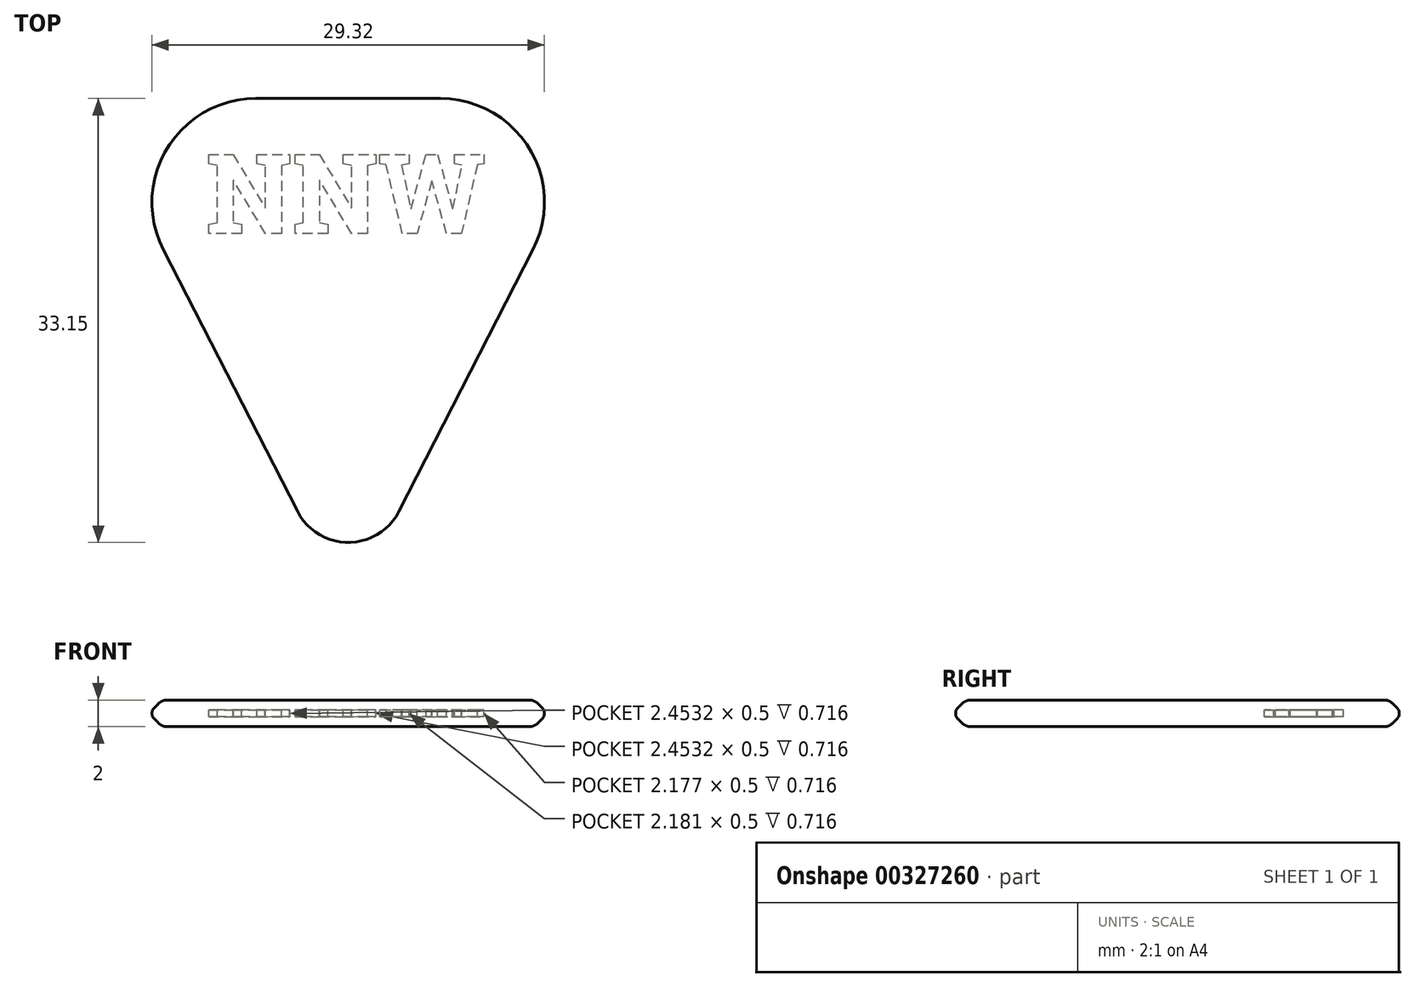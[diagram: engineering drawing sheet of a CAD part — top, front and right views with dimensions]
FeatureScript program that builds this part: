
annotation { "Feature Type Name" : "Feature", "Feature Type Description" : "" }
export const myFeature = defineFeature(function(context is Context, id is Id, definition is map)
    precondition{}
    {
        {
            var Q0;
            Q0=qCreatedBy(makeId("Top.planeOp"),FACE);
            var sketch = newSketch(context, id + "F0", { "sketchPlane" : qUnion([Q0])});
            skLineSegment(sketch, "E0", {"start": v(-6.9, 12.45) * mm, "end": v(6.9, 12.45) * mm});
            skLineSegment(sketch, "E1", {"start": v(14.03, 0.8) * mm, "end": v(4, -18.74) * mm});
            skLineSegment(sketch, "E2", {"start": v(-4, -18.74) * mm, "end": v(-14.03, 0.8) * mm});
            skPoint(sketch, "E3.visualSharp", {"position": v(-20, 12.45) * mm});
            skArc(sketch, "E3.filletArc", {"start": v(-6.9, 12.45) * mm, "mid": v(-13.73, 8.63) * mm, "end": v(-14.03, 0.8) * mm});
            skPoint(sketch, "E4.visualSharp", {"position": v(20, 12.45) * mm});
            skArc(sketch, "E4.filletArc", {"start": v(14.03, 0.8) * mm, "mid": v(13.73, 8.63) * mm, "end": v(6.9, 12.45) * mm});
            skPoint(sketch, "E5.visualSharp", {"position": v(0, -26.55) * mm});
            skArc(sketch, "E5.filletArc", {"start": v(-4, -18.74) * mm, "mid": v(0, -21.18) * mm, "end": v(4, -18.74) * mm});
            skSolve(sketch);
        }
        {
            var Q0;
            Q0=makeQuery(id+"F0.imprint","IMPRINT",FACE,{"disambiguationData":[TD([[makeQuery(id+"F0.imprint","IMPRINT",EDGE,{"derivedFrom":sQuery(id+"F0.wireOp",EDGE,"E0")}),-1.0]])]});
            extrude(context, id + "F1", {"entities" : qUnion([Q0]), "endBound" : BoundingType.SYMMETRIC, "depth" : 2 * mm});
        }
        {
            var Q0;
            Q0=makeQuery(id+"F1.opExtrude","CAP_EDGE",EDGE,{"disambiguationData":[OSD([sQuery(id+"F0.wireOp",EDGE,"E1")])],"isStart":false});
            var Q1;
            Q1=makeQuery(id+"F1.opExtrude","CAP_EDGE",EDGE,{"disambiguationData":[OSD([sQuery(id+"F0.wireOp",EDGE,"E1")])],"isStart":true});
            chamfer(context, id + "F2", {"entities" : qUnion([Q0, Q1]), "chamferType" : ChamferType.OFFSET_ANGLE, "width" : 1 * mm, "oppositeDirection" : false, "angle" : 45 * degree, "tangentPropagation" : true});
        }
        {
            var Q0;
            {var subQ0=sQuery(id+"F0.wireOp",EDGE,"E2");Q0=makeQuery(id+"F2.opChamfer","BLEND_EDGE",EDGE,{"blendedFrom":[makeQuery(id+"F1.opExtrude","CAP_EDGE",EDGE,{"disambiguationData":[OSD([subQ0])],"isStart":false}),makeQuery(id+"F1.opExtrude","CAP_FACE",FACE,{"disambiguationData":[OSD([sQuery(id+"F0.wireOp",EDGE,"E0"),sQuery(id+"F0.wireOp",EDGE,"E1"),subQ0,sQuery(id+"F0.wireOp",EDGE,"E3.filletArc"),sQuery(id+"F0.wireOp",EDGE,"E4.filletArc"),sQuery(id+"F0.wireOp",EDGE,"E5.filletArc")])],"isStart":false})],"blendedInto":[makeQuery(id+"F1.opExtrude","CAP_FACE",FACE,{"disambiguationData":[OSD([sQuery(id+"F0.wireOp",EDGE,"E0"),sQuery(id+"F0.wireOp",EDGE,"E1"),subQ0,sQuery(id+"F0.wireOp",EDGE,"E3.filletArc"),sQuery(id+"F0.wireOp",EDGE,"E4.filletArc"),sQuery(id+"F0.wireOp",EDGE,"E5.filletArc")])],"isStart":false})]});}
            var Q1;
            {var subQ0=sQuery(id+"F0.wireOp",EDGE,"E1");Q1=makeQuery(id+"F2.opChamfer","BLEND_EDGE",EDGE,{"blendedFrom":[makeQuery(id+"F1.opExtrude","CAP_EDGE",EDGE,{"disambiguationData":[OSD([subQ0])],"isStart":true}),makeQuery(id+"F1.opExtrude","CAP_FACE",FACE,{"disambiguationData":[OSD([sQuery(id+"F0.wireOp",EDGE,"E0"),subQ0,sQuery(id+"F0.wireOp",EDGE,"E2"),sQuery(id+"F0.wireOp",EDGE,"E3.filletArc"),sQuery(id+"F0.wireOp",EDGE,"E4.filletArc"),sQuery(id+"F0.wireOp",EDGE,"E5.filletArc")])],"isStart":true})],"blendedInto":[makeQuery(id+"F1.opExtrude","CAP_FACE",FACE,{"disambiguationData":[OSD([sQuery(id+"F0.wireOp",EDGE,"E0"),subQ0,sQuery(id+"F0.wireOp",EDGE,"E2"),sQuery(id+"F0.wireOp",EDGE,"E3.filletArc"),sQuery(id+"F0.wireOp",EDGE,"E4.filletArc"),sQuery(id+"F0.wireOp",EDGE,"E5.filletArc")])],"isStart":true})]});}
            fillet(context, id + "F3", {"entities" : qUnion([Q0, Q1]), "radius" : 1 * mm, "tangentPropagation" : true, "allowEdgeOverflow" : false});
        }
        {
            var Q0;
            Q0=qCreatedBy(makeId("Top.planeOp"),FACE);
            var sketch = newSketch(context, id + "F4", { "sketchPlane" : qUnion([Q0])});
            skText(sketch, "E6", { "text": "NNW", "fontName": "RobotoSlab-Bold.ttf"});
            const initialGuessF4  = {"E6": [-0.01064, 0.00212, 1, 0, 0.006]};
            skSetInitialGuess(sketch, initialGuessF4);
            skSolve(sketch);
        }
        {
            var Q0;
            Q0=qSketchRegion(id+"F4",true);
            extrude(context, id + "F5", {"entities" : qUnion([Q0]), "operationType" : NewBodyOperationType.REMOVE, "endBound" : BoundingType.SYMMETRIC, "oppositeDirection" : true, "depth" : 0.5 * mm});
        }
        {
            var Q0;
            {var subQ0=sQuery(id+"F0.wireOp",EDGE,"E2");Q0=makeQuery(id+"F2.opChamfer","BLEND_EDGE",EDGE,{"blendedFrom":[makeQuery(id+"F1.opExtrude","CAP_EDGE",EDGE,{"disambiguationData":[OSD([subQ0])],"isStart":true}),makeQuery(id+"F1.opExtrude","CAP_EDGE",EDGE,{"disambiguationData":[OSD([subQ0])],"isStart":false})],"blendedInto":[]});}
            fillet(context, id + "F6", {"entities" : qUnion([Q0]), "radius" : 0.6 * mm, "tangentPropagation" : true, "allowEdgeOverflow" : false});
        }
    });
